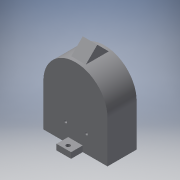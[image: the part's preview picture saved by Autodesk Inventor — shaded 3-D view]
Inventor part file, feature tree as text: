
AUTODESK INVENTOR PART (.ipt)
format: ipt  version: 2016 (Build 200138000, 138)  size: 160,768 bytes
history: native  units: in
note: dims shown in document units (in); Inventor stores cm internally (conversion verified against a paired STEP export)
features: extrude x7, sketch x6, reference x4, plane x1
ambient origin geometry x8: Origin, YZ Plane, XZ Plane, XY Plane, X Axis, Y Axis, Z Axis, Center Point
bodies: Solid1 (feature_tree)
feature tree (18):
  extrude  "Extrusion1"  Depth=0.4in TaperAngle=0.0deg
  extrude  "Extrusion2"  Depth=0.5in
  extrude  "Extrusion4"  Depth=0.4in TaperAngle=0.0deg
  extrude  "Extrusion5"  Depth=0.1378in
  extrude  "Extrusion6"  Depth=0.25in
  plane  "Work Plane1"
  extrude  "Extrusion7"  Depth=0.197in
  extrude  "Extrusion8"  Depth=1.0in
  sketch  "Sketch1"  dims[d1=1.0in d2=0.0in d4=0.4in d5=0.0in]
  reference  "Reference1"
  sketch  "Sketch2"  dims[d10=0.25in d11=0.5in]
  reference  "Reference2"
  sketch  "Sketch5"  dims[d12=0.197in d13=0.4in d14=0.0in]
  sketch  "Sketch6"  dims[d15=0.15in d16=0.1378in]
  sketch  "Sketch7"  dims[d17=0.4in d18=0.0in d19=0.25in]
  sketch  "Sketch8"  dims[d20=0.5in d21=0.197in d22=0.15in d23=0.1772in d24=0.4in d25=0.0in d26=0.25in d27=2.2in d28=-1.1in d29=0.1065in d30=0.787in d31=0.394in d32=0.394in d33=0.5in d34=0.0in d35=0.0394in d36=0.0394in d37=0.098in d38=0.098in d39=1.0in d40=0.0in]
  reference  "Reference3"
  reference  "Reference4"
